FCSTD DOCUMENT  (FreeCAD 0.20R)
Label: VESC_UI
License: All rights reserved
LicenseURL: http://en.wikipedia.org/wiki/All_rights_reserved
objects: App::Link×62, Part::Feature×36, App::Part×13, PartDesign::CoordinateSystem×1, Sketcher::SketchObject×1, Part::MultiFuse×1
note: 39 computed .brp shape members not serialized (recipe doc carries the construction recipe); baked Part::Feature solids carry a one-line shape summary decoded from their .brp

FEATURE [PartDesign::CoordinateSystem] Local_CS_365b
  AttacherType = Attacher::AttachEngine3D
FEATURE [Part::Feature] Pcb_365b
  shape: bbox 50 x 50 x 1.6 mm, 76 faces (baked)
FEATURE [Sketcher::SketchObject] PCB_Sketch_365b
  FullyConstrained = false
  sketch-geometry (8):
    g0: LineSegment StartX=164 StartY=-85 StartZ=0 EndX=164 EndY=-125 EndZ=0
    g1: LineSegment StartX=114 StartY=-125 StartZ=0 EndX=114 EndY=-85 EndZ=0
    g2: LineSegment StartX=163 StartY=-85 StartZ=0 EndX=164 EndY=-85 EndZ=0
    g3: LineSegment StartX=163 StartY=-75 StartZ=0 EndX=163 EndY=-85 EndZ=0
    g4: LineSegment StartX=114 StartY=-85 StartZ=0 EndX=115 EndY=-85 EndZ=0
    g5: LineSegment StartX=115 StartY=-85 StartZ=0 EndX=115 EndY=-75 EndZ=0
    g6: LineSegment StartX=115 StartY=-75 StartZ=0 EndX=163 EndY=-75 EndZ=0
    g7: LineSegment StartX=164 StartY=-125 StartZ=0 EndX=114 EndY=-125 EndZ=0
  constraints (8):
    c: Coincident(g1,g7)
    c: Coincident(g1,g4)
    c: Coincident(g4,g5)
    c: Coincident(g5,g6)
    c: Coincident(g2,g3)
    c: Coincident(g3,g6)
    c: Coincident(g0,g7)
    c: Coincident(g0,g2)
FEATURE [App::Part] Board_Geoms_365b
  Group = -> [Local_CS_365b,Pcb_365b,PCB_Sketch_365b]
  Origin = -> Origin
FEATURE [Part::Feature] Shape  label="D6_LED_D5.0mm_Horizontal_O1.27mm_Z3.0mm_Clear_00005fc409b9"
  Placement = pos=(159.7,-79,0) rot=(0,0,1;3.14159rad)
  shape: bbox 5.4 x 10.17 x 7.9 mm, 33 faces (baked)
FEATURE [App::Link] D6_LED_D5_0mm_Horizontal_O1_27mm_Z3_0mm_Clear_00005fc409b9_ln_  label="D3_LED_D5.0mm_Horizontal_O1.27mm_Z3.0mm_Clear_00005fc47b63"
  LinkPlacement = pos=(136.5,-79,0) rot=(0,0,1;3.14159rad)
  LinkedObject = -> Shape
  Placement = pos=(136.5,-79,0) rot=(0,0,1;3.14159rad)
FEATURE [Part::Feature] Part__Feature  label="R_0402"
  shape: bbox 1 x 0.5 x 0.35 mm, 85 faces (baked)
FEATURE [App::Part] ASSEMBLY  label="R4_ASSEMBLY_00005fc47db6"
  Group = -> [Part__Feature]
  Origin = -> Origin008
  Placement = pos=(151.9,-81.2,0) rot=(0,0,-1;1.5708rad)
FEATURE [App::Link] R4_ASSEMBLY_00005fc47db6_ln_  label="R1_ASSEMBLY_00005fc47eb7"
  LinkPlacement = pos=(125.2,-81.7,0) rot=(0,0,1;0rad)
  LinkedObject = -> ASSEMBLY
  Placement = pos=(125.2,-81.7,0) rot=(0,0,1;0rad)
FEATURE [App::Link] R4_ASSEMBLY_00005fc47db6_ln_001  label="R6_ASSEMBLY_00005fc47f75"
  LinkPlacement = pos=(159.7,-81.2,0) rot=(0,0,-1;1.5708rad)
  LinkedObject = -> ASSEMBLY
  Placement = pos=(159.7,-81.2,0) rot=(0,0,-1;1.5708rad)
FEATURE [Part::Feature] Shape001  label="C12_C_0402_00005fc4d41e"
  Placement = pos=(144.5,-107.1,0) rot=(0,0,1;0rad)
  shape: bbox 1 x 0.5 x 0.5 mm, 28 faces (baked)
FEATURE [App::Link] C12_C_0402_00005fc4d41e_ln_  label="C19_C_0402_00005fc4d495"
  LinkPlacement = pos=(149.7,-99,0) rot=(0,0,1;1.5708rad)
  LinkedObject = -> Shape001
  Placement = pos=(149.7,-99,0) rot=(0,0,1;1.5708rad)
FEATURE [App::Link] D6_LED_D5_0mm_Horizontal_O1_27mm_Z3_0mm_Clear_00005fc409b9_ln_001  label="D1_LED_D5.0mm_Horizontal_O1.27mm_Z3.0mm_Clear_00005fc4d50c"
  LinkPlacement = pos=(120.9,-79,0) rot=(0,0,1;3.14159rad)
  LinkedObject = -> Shape
  Placement = pos=(120.9,-79,0) rot=(0,0,1;3.14159rad)
FEATURE [App::Link] D6_LED_D5_0mm_Horizontal_O1_27mm_Z3_0mm_Clear_00005fc409b9_ln_002  label="D2_LED_D5.0mm_Horizontal_O1.27mm_Z3.0mm_Clear_00005fc4d51e"
  LinkPlacement = pos=(128.69,-79,0) rot=(0,0,1;3.14159rad)
  LinkedObject = -> Shape
  Placement = pos=(128.69,-79,0) rot=(0,0,1;3.14159rad)
FEATURE [App::Link] D6_LED_D5_0mm_Horizontal_O1_27mm_Z3_0mm_Clear_00005fc409b9_ln_003  label="D4_LED_D5.0mm_Horizontal_O1.27mm_Z3.0mm_Clear_00005fc4d542"
  LinkPlacement = pos=(144.29,-79,0) rot=(0,0,1;3.14159rad)
  LinkedObject = -> Shape
  Placement = pos=(144.29,-79,0) rot=(0,0,1;3.14159rad)
FEATURE [App::Link] D6_LED_D5_0mm_Horizontal_O1_27mm_Z3_0mm_Clear_00005fc409b9_ln_004  label="D5_LED_D5.0mm_Horizontal_O1.27mm_Z3.0mm_Clear_00005fc4d554"
  LinkPlacement = pos=(151.9,-79,0) rot=(0,0,1;3.14159rad)
  LinkedObject = -> Shape
  Placement = pos=(151.9,-79,0) rot=(0,0,1;3.14159rad)
FEATURE [Part::Feature] Part__Feature001  label="User_Library-SOD-523_SCD80_SC-79"
  shape: bbox 1.8 x 0.8989 x 0.801 mm, 67 faces (baked)
FEATURE [App::Part] ASSEMBLY001  label="D10_ASSEMBLY_00005fc4d5c1"
  Group = -> [Part__Feature001]
  Origin = -> Origin009
  Placement = pos=(137.2,-93.9,0) rot=(0,0,-1;1.5708rad)
FEATURE [Part::Feature] Shape002  label="J5_JST_B5B_PH_K_00005fc4d681"
  Placement = pos=(155.4,-85.75,0) rot=(0,0,1;3.14159rad)
  shape: bbox 11.9 x 4.55 x 9.4 mm, 177 faces (baked)
FEATURE [Part::Feature] Shape003  label="J6_JST_B4B_PH_K_00005fc4d6a3"
  Placement = pos=(149.5,-115,0) rot=(0,0,1;0rad)
  shape: bbox 9.9 x 4.55 x 9.4 mm, 149 faces (baked)
FEATURE [App::Link] R4_ASSEMBLY_00005fc47db6_ln_002  label="R3_ASSEMBLY_00005fc4d7d4"
  LinkPlacement = pos=(133.15,-103.9,0) rot=(0,0,1;1.5708rad)
  LinkedObject = -> ASSEMBLY
  Placement = pos=(133.15,-103.9,0) rot=(0,0,1;1.5708rad)
FEATURE [App::Link] R4_ASSEMBLY_00005fc47db6_ln_003  label="R5_ASSEMBLY_00005fc4d7f6"
  LinkPlacement = pos=(142.5,-86.7,0) rot=(0,0,1;3.14159rad)
  LinkedObject = -> ASSEMBLY
  Placement = pos=(142.5,-86.7,0) rot=(0,0,1;3.14159rad)
FEATURE [App::Link] R4_ASSEMBLY_00005fc47db6_ln_004  label="R12_ASSEMBLY_00005fc4d86d"
  LinkPlacement = pos=(144.5,-118.8,0) rot=(0,0,1;3.14159rad)
  LinkedObject = -> ASSEMBLY
  Placement = pos=(144.5,-118.8,0) rot=(0,0,1;3.14159rad)
FEATURE [Part::Feature] Shape004  label="U2_QFN_48_1EP_7x7mm_P05mm_EP56x56mm_00005fc4f150"
  Placement = pos=(152.25,-104.5,0) rot=(0,0,1;0rad)
  shape: bbox 7 x 7 x 1.1 mm, 302 faces (baked)
FEATURE [Part::Feature] Shape005  label="J8_JST_B2B_PH_K_00005fc5adee"
  Placement = pos=(131.5,-85.75,0) rot=(0,0,1;3.14159rad)
  shape: bbox 5.9 x 4.55 x 9.4 mm, 93 faces (baked)
FEATURE [Part::Feature] Shape006  label="J3_JST_B7B_PH_K_00005fcd457f"
  Placement = pos=(131.5,-115,0) rot=(0,0,1;0rad)
  shape: bbox 15.9 x 4.55 x 9.4 mm, 233 faces (baked)
FEATURE [App::Link] R4_ASSEMBLY_00005fc47db6_ln_005  label="R2_ASSEMBLY_00005fcd8532"
  LinkPlacement = pos=(153.6,-90.4,0) rot=(0,0,-1;1.5708rad)
  LinkedObject = -> ASSEMBLY
  Placement = pos=(153.6,-90.4,0) rot=(0,0,-1;1.5708rad)
FEATURE [App::Link] R4_ASSEMBLY_00005fc47db6_ln_006  label="R14_ASSEMBLY_00005fd9860c"
  LinkPlacement = pos=(133.4,-96.72,0) rot=(0,0,1;0rad)
  LinkedObject = -> ASSEMBLY
  Placement = pos=(133.4,-96.72,0) rot=(0,0,1;0rad)
FEATURE [Part::Feature] Shape007  label="C2_C_0603_00005fda97ac"
  Placement = pos=(148.5,-98.6,0) rot=(0,0,1;1.5708rad)
  shape: bbox 0.81 x 1.6 x 0.78 mm, 28 faces (baked)
FEATURE [App::Link] R4_ASSEMBLY_00005fc47db6_ln_007  label="R9_ASSEMBLY_00005fda9985"
  LinkPlacement = pos=(118.7,-118.8,0) rot=(0,0,1;3.14159rad)
  LinkedObject = -> ASSEMBLY
  Placement = pos=(118.7,-118.8,0) rot=(0,0,1;3.14159rad)
FEATURE [App::Link] R4_ASSEMBLY_00005fc47db6_ln_008  label="R7_ASSEMBLY_00005fda9a71"
  LinkPlacement = pos=(141.7,-105.5,0) rot=(0,0,1;3.14159rad)
  LinkedObject = -> ASSEMBLY
  Placement = pos=(141.7,-105.5,0) rot=(0,0,1;3.14159rad)
FEATURE [App::Link] J8_JST_B2B_PH_K_00005fc5adee_ln_  label="J9_JST_B2B_PH_K_00005fdfc953"
  LinkPlacement = pos=(138.55,-85.75,0) rot=(0,0,1;3.14159rad)
  LinkedObject = -> Shape005
  Placement = pos=(138.55,-85.75,0) rot=(0,0,1;3.14159rad)
FEATURE [App::Link] C12_C_0402_00005fc4d41e_ln_001  label="C18_C_0402_00005fe035f1"
  LinkPlacement = pos=(145.5,-120,0) rot=(0,0,1;3.14159rad)
  LinkedObject = -> Shape001
  Placement = pos=(145.5,-120,0) rot=(0,0,1;3.14159rad)
FEATURE [App::Link] R4_ASSEMBLY_00005fc47db6_ln_009  label="R8_ASSEMBLY_00005fe089c1"
  LinkPlacement = pos=(143.5,-105.5,0) rot=(0,0,1;3.14159rad)
  LinkedObject = -> ASSEMBLY
  Placement = pos=(143.5,-105.5,0) rot=(0,0,1;3.14159rad)
FEATURE [App::Link] C2_C_0603_00005fda97ac_ln_  label="C1_C_0603_00005fe089f1"
  LinkPlacement = pos=(144.1,-99.8,0) rot=(0,0,-1;1.5708rad)
  LinkedObject = -> Shape007
  Placement = pos=(144.1,-99.8,0) rot=(0,0,-1;1.5708rad)
FEATURE [Part::Feature] Shape008  label="Q2_SOT_23_00005fe08a28"
  Placement = pos=(143,-84.225,0) rot=(0,0,1;1.5708rad)
  shape: bbox 3 x 2.5 x 1.2 mm, 76 faces (baked)
FEATURE [Part::Feature] Shape009  label="U3_SOIC_8_39x49mm_P127mm_00005fe272fe"
  Placement = pos=(154.3,-95.6,0) rot=(0,0,-1;1.5708rad)
  shape: bbox 4.9 x 6 x 1.75 mm, 156 faces (baked)
FEATURE [App::Link] C12_C_0402_00005fc4d41e_ln_002  label="C9_C_0402_00005fe3d5eb"
  LinkPlacement = pos=(161.1,-99.1,0) rot=(0,0,1;1.5708rad)
  LinkedObject = -> Shape001
  Placement = pos=(161.1,-99.1,0) rot=(0,0,1;1.5708rad)
FEATURE [App::Link] C12_C_0402_00005fc4d41e_ln_003  label="C15_C_0402_00005fe3d61d"
  LinkPlacement = pos=(140,-104.6,0) rot=(0,0,-1;1.5708rad)
  LinkedObject = -> Shape001
  Placement = pos=(140,-104.6,0) rot=(0,0,-1;1.5708rad)
FEATURE [App::Link] C12_C_0402_00005fc4d41e_ln_004  label="C20_C_0402_00005fe3d65e"
  LinkPlacement = pos=(157.8,-101.6,0) rot=(0,0,1;3.14159rad)
  LinkedObject = -> Shape001
  Placement = pos=(157.8,-101.6,0) rot=(0,0,1;3.14159rad)
FEATURE [App::Link] C12_C_0402_00005fc4d41e_ln_005  label="C21_C_0402_00005fe3d66f"
  LinkPlacement = pos=(155.2,-110,0) rot=(0,0,1;1.5708rad)
  LinkedObject = -> Shape001
  Placement = pos=(155.2,-110,0) rot=(0,0,1;1.5708rad)
FEATURE [App::Link] C12_C_0402_00005fc4d41e_ln_006  label="C24_C_0402_00005fe3d6d0"
  LinkPlacement = pos=(150.7,-98.3,0) rot=(0,0,1;1.5708rad)
  LinkedObject = -> Shape001
  Placement = pos=(150.7,-98.3,0) rot=(0,0,1;1.5708rad)
FEATURE [Part::Feature] Part__Feature002  label="User_Library-DSK-3R3H"
  shape: bbox 11.7 x 7.361 x 2.8 mm, 36 faces (baked)
FEATURE [App::Part] ASSEMBLY002  label="C22_ASSEMBLY_00005fe82f86"
  Group = -> [Part__Feature002]
  Origin = -> Origin010
  Placement = pos=(144.4,-92.1,0) rot=(0,0,1;0rad)
FEATURE [App::Link] C12_C_0402_00005fc4d41e_ln_007  label="C10_C_0402_00005fe869a5"
  LinkPlacement = pos=(116.8,-100.5,0) rot=(0,0,-1;1.5708rad)
  LinkedObject = -> Shape001
  Placement = pos=(116.8,-100.5,0) rot=(0,0,-1;1.5708rad)
FEATURE [App::Link] R4_ASSEMBLY_00005fc47db6_ln_010  label="R17_ASSEMBLY_00005fe87df3"
  LinkPlacement = pos=(118,-100.3,0) rot=(0,0,-1;1.5708rad)
  LinkedObject = -> ASSEMBLY
  Placement = pos=(118,-100.3,0) rot=(0,0,-1;1.5708rad)
FEATURE [App::Link] R4_ASSEMBLY_00005fc47db6_ln_011  label="R18_ASSEMBLY_00005fe8a4be"
  LinkPlacement = pos=(159.9,-99.3,0) rot=(0,0,1;1.5708rad)
  LinkedObject = -> ASSEMBLY
  Placement = pos=(159.9,-99.3,0) rot=(0,0,1;1.5708rad)
FEATURE [App::Link] R4_ASSEMBLY_00005fc47db6_ln_012  label="R10_ASSEMBLY_000060319659"
  LinkPlacement = pos=(128.7,-81.2,0) rot=(0,0,-1;1.5708rad)
  LinkedObject = -> ASSEMBLY
  Placement = pos=(128.7,-81.2,0) rot=(0,0,-1;1.5708rad)
FEATURE [App::Link] R4_ASSEMBLY_00005fc47db6_ln_013  label="R11_ASSEMBLY_00006031966a"
  LinkPlacement = pos=(136.5,-81.2,0) rot=(0,0,-1;1.5708rad)
  LinkedObject = -> ASSEMBLY
  Placement = pos=(136.5,-81.2,0) rot=(0,0,-1;1.5708rad)
FEATURE [App::Link] R4_ASSEMBLY_00005fc47db6_ln_014  label="R15_ASSEMBLY_0000603196f9"
  LinkPlacement = pos=(144.3,-81.2,0) rot=(0,0,-1;1.5708rad)
  LinkedObject = -> ASSEMBLY
  Placement = pos=(144.3,-81.2,0) rot=(0,0,-1;1.5708rad)
FEATURE [App::Link] C12_C_0402_00005fc4d41e_ln_008  label="C23_C_0402_00006031ae9b"
  LinkPlacement = pos=(132.5,-120,0) rot=(0,0,1;3.14159rad)
  LinkedObject = -> Shape001
  Placement = pos=(132.5,-120,0) rot=(0,0,1;3.14159rad)
FEATURE [App::Link] Q2_SOT_23_00005fe08a28_ln_  label="Q1_SOT_23_00006031d33a"
  LinkPlacement = pos=(156,-89.9,0) rot=(0,0,1;1.5708rad)
  LinkedObject = -> Shape008
  Placement = pos=(156,-89.9,0) rot=(0,0,1;1.5708rad)
FEATURE [App::Link] C12_C_0402_00005fc4d41e_ln_009  label="C6_C_0402_00006031dfa0"
  LinkPlacement = pos=(117.2,-82.2,0) rot=(0,0,1;1.5708rad)
  LinkedObject = -> Shape001
  Placement = pos=(117.2,-82.2,0) rot=(0,0,1;1.5708rad)
FEATURE [App::Link] C12_C_0402_00005fc4d41e_ln_010  label="C28_C_0402_7a42c22551de"
  LinkPlacement = pos=(133.6,-94.1,0) rot=(0,0,1;0rad)
  LinkedObject = -> Shape001
  Placement = pos=(133.6,-94.1,0) rot=(0,0,1;0rad)
FEATURE [Part::Feature] Part__Feature003  label="Fusion"
  shape: bbox 0.71 x 0.3 x 10.57 mm, 38 faces (baked)
FEATURE [Part::Feature] Part__Feature004  label="Fusion001"
  shape: bbox 0.71 x 0.3 x 10.57 mm, 38 faces (baked)
FEATURE [Part::Feature] Part__Feature005  label="Fusion002"
  shape: bbox 6.039 x 9.415 x 6.039 mm, 113 faces (baked)
FEATURE [Part::Feature] Part__Feature006  label="Fusion003"
  shape: bbox 8.486 x 6.647 x 10.59 mm, 369 faces (baked)
FEATURE [App::Part] Fusion  label="SW1_Fusion004_86ee7cc48252"
  Group = -> [Part__Feature003,Part__Feature004,Part__Feature005,Part__Feature006]
  Origin = -> Origin011
  Placement = pos=(119.65,-121.198,0) rot=(0,0,1;0rad)
FEATURE [Part::Feature] Part__Feature007  label="SOD_123"
  shape: bbox 3.706 x 1.556 x 1.356 mm, 130 faces (baked)
FEATURE [App::Part] ASSEMBLY003  label="D9_ASSEMBLY_55e7b5fbd714"
  Group = -> [Part__Feature007]
  Origin = -> Origin012
  Placement = pos=(138.3,-103.7,0) rot=(0,0,1;1.5708rad)
FEATURE [App::Link] C2_C_0603_00005fda97ac_ln_001  label="C4_C_0603_22664b955136"
  LinkPlacement = pos=(134.4,-108,0) rot=(0,0,1;0rad)
  LinkedObject = -> Shape007
  Placement = pos=(134.4,-108,0) rot=(0,0,1;0rad)
FEATURE [App::Link] C2_C_0603_00005fda97ac_ln_002  label="C26_C_0603_8afad56edf02"
  LinkPlacement = pos=(134,-95.3,0) rot=(0,0,1;3.14159rad)
  LinkedObject = -> Shape007
  Placement = pos=(134,-95.3,0) rot=(0,0,1;3.14159rad)
FEATURE [App::Link] D10_ASSEMBLY_00005fc4d5c1_ln_  label="D8_ASSEMBLY_1e14f5cbb1b0"
  LinkPlacement = pos=(134.6,-100,0) rot=(0,0,1;0rad)
  LinkedObject = -> ASSEMBLY001
  Placement = pos=(134.6,-100,0) rot=(0,0,1;0rad)
FEATURE [App::Link] C2_C_0603_00005fda97ac_ln_003  label="C29_C_0603_dc05a1d7fd29"
  LinkPlacement = pos=(146.3,-105.9,0) rot=(0,0,1;1.5708rad)
  LinkedObject = -> Shape007
  Placement = pos=(146.3,-105.9,0) rot=(0,0,1;1.5708rad)
FEATURE [App::Link] R4_ASSEMBLY_00005fc47db6_ln_015  label="R16_ASSEMBLY_b4604c19602c"
  LinkPlacement = pos=(131.5,-118.8,0) rot=(0,0,1;3.14159rad)
  LinkedObject = -> ASSEMBLY
  Placement = pos=(131.5,-118.8,0) rot=(0,0,1;3.14159rad)
FEATURE [App::Link] C12_C_0402_00005fc4d41e_ln_011  label="C17_C_0402_fb0bf1e9839c"
  LinkPlacement = pos=(119.7,-120,0) rot=(0,0,1;3.14159rad)
  LinkedObject = -> Shape001
  Placement = pos=(119.7,-120,0) rot=(0,0,1;3.14159rad)
FEATURE [App::Link] SW1_Fusion004_86ee7cc48252_ln_  label="SW2_Fusion004_8063fc3dec15"
  LinkPlacement = pos=(132.55,-121.198,0) rot=(0,0,1;0rad)
  LinkedObject = -> Fusion
  Placement = pos=(132.55,-121.198,0) rot=(0,0,1;0rad)
FEATURE [App::Link] C2_C_0603_00005fda97ac_ln_004  label="C8_C_0603_a34f24e8dba8"
  LinkPlacement = pos=(134.4,-105.5,0) rot=(0,0,1;0rad)
  LinkedObject = -> Shape007
  Placement = pos=(134.4,-105.5,0) rot=(0,0,1;0rad)
FEATURE [App::Link] C2_C_0603_00005fda97ac_ln_005  label="C16_C_0603_b78d1be87fde"
  LinkPlacement = pos=(137.7,-108,0) rot=(0,0,1;0rad)
  LinkedObject = -> Shape007
  Placement = pos=(137.7,-108,0) rot=(0,0,1;0rad)
FEATURE [App::Link] C12_C_0402_00005fc4d41e_ln_012  label="C32_C_0402_2e255aa7799a"
  LinkPlacement = pos=(128.2,-116.1,0) rot=(0,0,-1;1.5708rad)
  LinkedObject = -> Shape001
  Placement = pos=(128.2,-116.1,0) rot=(0,0,-1;1.5708rad)
FEATURE [App::Link] C12_C_0402_00005fc4d41e_ln_013  label="C13_C_0402_6ca84abd0f64"
  LinkPlacement = pos=(131.4,-88.5,0) rot=(0,0,1;0rad)
  LinkedObject = -> Shape001
  Placement = pos=(131.4,-88.5,0) rot=(0,0,1;0rad)
FEATURE [App::Link] SW1_Fusion004_86ee7cc48252_ln_001  label="SW3_Fusion004_aafa09688bf5"
  LinkPlacement = pos=(145.45,-121.198,0) rot=(0,0,1;0rad)
  LinkedObject = -> Fusion
  Placement = pos=(145.45,-121.198,0) rot=(0,0,1;0rad)
FEATURE [Part::Feature] Shape010  label="SW5_Y97M01810FP_034017bd4c7c"
  Placement = pos=(144.1,-109.7,0) rot=(0,0,1;0rad)
  shape: bbox 4.575 x 3.2 x 2.5 mm, 198 faces (baked)
FEATURE [App::Link] C12_C_0402_00005fc4d41e_ln_014  label="C11_C_0402_4ad183609576"
  LinkPlacement = pos=(142.7,-87.9,0) rot=(0,0,1;3.14159rad)
  LinkedObject = -> Shape001
  Placement = pos=(142.7,-87.9,0) rot=(0,0,1;3.14159rad)
FEATURE [App::Link] C2_C_0603_00005fda97ac_ln_006  label="C7_C_0603_60f7236dff97"
  LinkPlacement = pos=(135.15,-104.1,0) rot=(0,0,1;0rad)
  LinkedObject = -> Shape007
  Placement = pos=(135.15,-104.1,0) rot=(0,0,1;0rad)
FEATURE [Part::Feature] Shape011  label="C5_C_1210_2f675413b2eb"
  Placement = pos=(120.1,-82.7,0) rot=(0,0,1;0rad)
  shape: bbox 3.2 x 2.5 x 2.5 mm, 28 faces (baked)
FEATURE [App::Link] R4_ASSEMBLY_00005fc47db6_ln_016  label="R19_ASSEMBLY_7794922f1ccb"
  LinkPlacement = pos=(157.3,-118.8,0) rot=(0,0,1;3.14159rad)
  LinkedObject = -> ASSEMBLY
  Placement = pos=(157.3,-118.8,0) rot=(0,0,1;3.14159rad)
FEATURE [App::Link] C5_C_1210_2f675413b2eb_ln_  label="C14_C_1210_ab1befe7a3cb"
  LinkPlacement = pos=(134.8,-89.8,0) rot=(0,0,1;0rad)
  LinkedObject = -> Shape011
  Placement = pos=(134.8,-89.8,0) rot=(0,0,1;0rad)
FEATURE [App::Link] C2_C_0603_00005fda97ac_ln_007  label="C30_C_0603_d0aa65038aa7"
  LinkPlacement = pos=(154,-110.4,0) rot=(0,0,-1;1.5708rad)
  LinkedObject = -> Shape007
  Placement = pos=(154,-110.4,0) rot=(0,0,-1;1.5708rad)
FEATURE [App::Link] C12_C_0402_00005fc4d41e_ln_015  label="C33_C_0402_8957ca9d23cc"
  LinkPlacement = pos=(131.6,-111.7,0) rot=(0,0,1;0rad)
  LinkedObject = -> Shape001
  Placement = pos=(131.6,-111.7,0) rot=(0,0,1;0rad)
FEATURE [App::Link] C12_C_0402_00005fc4d41e_ln_016  label="C25_C_0402_143f9b56fd85"
  LinkPlacement = pos=(158.3,-120,0) rot=(0,0,1;3.14159rad)
  LinkedObject = -> Shape001
  Placement = pos=(158.3,-120,0) rot=(0,0,1;3.14159rad)
FEATURE [App::Link] C5_C_1210_2f675413b2eb_ln_001  label="C35_C_1210_d1765295fe0d"
  LinkPlacement = pos=(135.1,-110.9,0) rot=(0,0,1;0rad)
  LinkedObject = -> Shape011
  Placement = pos=(135.1,-110.9,0) rot=(0,0,1;0rad)
FEATURE [App::Link] C12_C_0402_00005fc4d41e_ln_017  label="C3_C_0402_883dc675ad7b"
  LinkPlacement = pos=(134.2,-106.8,0) rot=(0,0,1;3.14159rad)
  LinkedObject = -> Shape001
  Placement = pos=(134.2,-106.8,0) rot=(0,0,1;3.14159rad)
FEATURE [App::Link] SW1_Fusion004_86ee7cc48252_ln_002  label="SW4_Fusion004_73c84f075683"
  LinkPlacement = pos=(158.35,-121.198,0) rot=(0,0,1;0rad)
  LinkedObject = -> Fusion
  Placement = pos=(158.35,-121.198,0) rot=(0,0,1;0rad)
FEATURE [App::Link] R4_ASSEMBLY_00005fc47db6_ln_017  label="R20_ASSEMBLY_0f30f15fadaa"
  LinkPlacement = pos=(158.6,-97,0) rot=(0,0,1;0rad)
  LinkedObject = -> ASSEMBLY
  Placement = pos=(158.6,-97,0) rot=(0,0,1;0rad)
FEATURE [Part::Feature] Part__Feature008  label="Pad001_sp_sp"
  shape: bbox 4.06 x 4.06 x 1 mm, 30 faces (baked)
FEATURE [Part::Feature] Part__Feature009  label="Pad001_sp_sp001"
  shape: bbox 4.45 x 2 x 0.6 mm, 22 faces (baked)
FEATURE [Part::Feature] Part__Feature010  label="Pad001_sp_sp002"
  shape: bbox 0.698 x 0.9396 x 0.01 mm, 16 faces (baked)
FEATURE [Part::Feature] Part__Feature011  label="Pad001_sp_sp003"
  shape: bbox 0.6443 x 0.9933 x 0.01 mm, 18 faces (baked)
FEATURE [Part::Feature] Part__Feature012  label="Pad001_sp_sp004"
  shape: bbox 0.5369 x 0.9396 x 0.01 mm, 13 faces (baked)
FEATURE [Part::Feature] Part__Feature013  label="Pad001_sp_sp005"
  shape: bbox 0.5956 x 0.9664 x 0.01 mm, 23 faces (baked)
FEATURE [App::Part] Pad001_sp_sp  label="L1_Pad001_sp_sp006_c6f1f3d44618"
  Group = -> [Part__Feature008,Part__Feature009,Part__Feature010,Part__Feature011,Part__Feature012,Part__Feature013]
  Origin = -> Origin013
  Placement = pos=(140.1,-98.9,0) rot=(0,0,1;3.14159rad)
FEATURE [App::Link] C5_C_1210_2f675413b2eb_ln_002  label="C34_C_1210_a59ac0eebc9e"
  LinkPlacement = pos=(126.1,-118.2,0) rot=(0,0,-1;1.5708rad)
  LinkedObject = -> Shape011
  Placement = pos=(126.1,-118.2,0) rot=(0,0,-1;1.5708rad)
FEATURE [App::Link] D10_ASSEMBLY_00005fc4d5c1_ln_001  label="D7_ASSEMBLY_00572e80b321"
  LinkPlacement = pos=(134.6,-101.5,0) rot=(0,0,1;3.14159rad)
  LinkedObject = -> ASSEMBLY001
  Placement = pos=(134.6,-101.5,0) rot=(0,0,1;3.14159rad)
FEATURE [App::Link] C2_C_0603_00005fda97ac_ln_008  label="C27_C_0603_f4fdf8eb46a9"
  LinkPlacement = pos=(134,-92.9,0) rot=(0,0,1;0rad)
  LinkedObject = -> Shape007
  Placement = pos=(134,-92.9,0) rot=(0,0,1;0rad)
FEATURE [App::Link] C12_C_0402_00005fc4d41e_ln_018  label="C31_C_0402_ef0efa938b0f"
  LinkPlacement = pos=(146.3,-103.3,0) rot=(0,0,-1;1.5708rad)
  LinkedObject = -> Shape001
  Placement = pos=(146.3,-103.3,0) rot=(0,0,-1;1.5708rad)
FEATURE [App::Part] Top_365b
  Group = -> [Shape,D6_LED_D5_0mm_Horizontal_O1_27mm_Z3_0mm_Clear_00005fc409b9_ln_,ASSEMBLY,R4_ASSEMBLY_00005fc47db6_ln_,R4_ASSEMBLY_00005fc47db6_ln_001,Shape001,C12_C_0402_00005fc4d41e_ln_,D6_LED_D5_0mm_Horizontal_O1_27mm_Z3_0mm_Clear_00005fc409b9_ln_001,D6_LED_D5_0mm_Horizontal_O1_27mm_Z3_0mm_Clear_00005fc409b9_ln_002,D6_LED_D5_0mm_Horizontal_O1_27mm_Z3_0mm_Clear_00005fc409b9_ln_003,+69 more]
  Origin = -> Origin003
FEATURE [Part::Feature] Shape012  label="J1_TO-92Flat_00005fe84a49"
  Placement = pos=(115.25,-101,-1.6) rot=(0.707107,0.707107,0;3.14159rad)
  shape: bbox 1.52 x 4 x 7.55 mm, 49 faces (baked)
FEATURE [Part::Feature] Part__Feature014  label="R_LDR_4.9x4.2mm_P2.54mm_Vertical"
  shape: bbox 4.9 x 4.2 x 7 mm, 14 faces (baked)
FEATURE [Part::Feature] Part__Feature015  label="R_LDR_4.9x4.2mm_P2.54mm_Vertical001"
  shape: bbox 2.45 x 3.78 x 0.05 mm, 42 faces (baked)
FEATURE [App::Part] R_LDR_4_9x4_2mm_P2_54mm_Vertical  label="R13_R_LDR_4.9x4.2mm_P2.54mm_Vertical002_00005fe84d35"
  Group = -> [Part__Feature014,Part__Feature015]
  Origin = -> Origin014
  Placement = pos=(159.1,-92.3,-1.6) rot=(0.707107,-0.707107,0;3.14159rad)
FEATURE [App::Link] J1_TO_92Flat_00005fe84a49_ln_  label="J2_TO-92Flat_00005fe85267"
  LinkPlacement = pos=(162.75,-98.5,-1.6) rot=(0.707107,-0.707107,0;3.14159rad)
  LinkedObject = -> Shape012
  Placement = pos=(162.75,-98.5,-1.6) rot=(0.707107,-0.707107,0;3.14159rad)
FEATURE [Part::Feature] Part__Feature016  label="SSD1351_Connector_v3_cp006_cp"
  shape: bbox 21.6 x 5.2 x 2.05 mm, 796 faces (baked)
FEATURE [Part::Feature] Part__Feature017  label="SSD1351_Connector_v3_cp006_cp001"
  shape: bbox 33.8 x 34 x 0.8 mm, 6 faces (baked)
FEATURE [Part::Feature] Part__Feature018  label="SSD1351_Connector_v3_cp006_cp002"
  shape: bbox 33.8 x 31 x 0.8 mm, 6 faces (baked)
FEATURE [Part::Feature] Part__Feature019  label="SSD1351_Connector_v3_cp006_cp003"
  shape: bbox 27.83 x 7.4 x 3.6 mm, 26 faces (baked)
FEATURE [Part::Feature] Part__Feature020  label="SSD1351_Connector_v3_cp006_cp004"
  shape: bbox 15.5 x 4 x 0.25 mm, 8 faces (baked)
FEATURE [Part::Feature] Part__Feature021  label="SSD1351_Connector_v3_cp006_cp005"
  shape: bbox 26.86 x 26.86 x 0.01 mm, 6 faces (baked)
FEATURE [App::Part] SSD1351_Connector_v3_cp006_cp  label="K1_SSD1351_Connector_v3_cp006_cp006_146d0b559c04"
  Group = -> [Part__Feature016,Part__Feature017,Part__Feature018,Part__Feature019,Part__Feature020,Part__Feature021]
  Origin = -> Origin015
  Placement = pos=(125.581,-99.975,-1.6) rot=(0.707107,0.707107,0;3.14159rad)
FEATURE [App::Part] Bot_365b
  Group = -> [Shape012,R_LDR_4_9x4_2mm_P2_54mm_Vertical,J1_TO_92Flat_00005fe84a49_ln_,SSD1351_Connector_v3_cp006_cp]
  Origin = -> Origin004
FEATURE [App::Part] Step_Models_365b
  Group = -> [Top_365b,Bot_365b]
  Origin = -> Origin002
FEATURE [App::Part] Board_365b  label="VESC_UI"
  Group = -> [Board_Geoms_365b,Step_Models_365b]
  Origin = -> Origin001
FEATURE [Part::MultiFuse] Fusion001  label="Fusion004"
  Shapes = -> [Step_Models_365b,Board_Geoms_365b]
